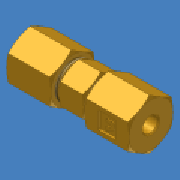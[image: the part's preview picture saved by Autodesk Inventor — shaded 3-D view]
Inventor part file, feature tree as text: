
AUTODESK INVENTOR PART (.ipt)
format: ipt  version: 2017.1 (Build 211199000, 199)  size: 289,792 bytes
history: native  units: in
note: dims shown in document units (in); Inventor stores cm internally (conversion verified against a paired STEP export)
features: other x2, sketch x1, imported_body x1
ambient origin geometry x8: Origin, YZ Plane, XZ Plane, XY Plane, X Axis, Y Axis, Z Axis, Center Point
bodies: Solid1 (feature_tree)
feature tree (4):
  other  "Table"
  other  "Union 62C.ipt"
  sketch  "Sketch1"
  imported_body  "DerivedBody::Union 62C.ipt"
